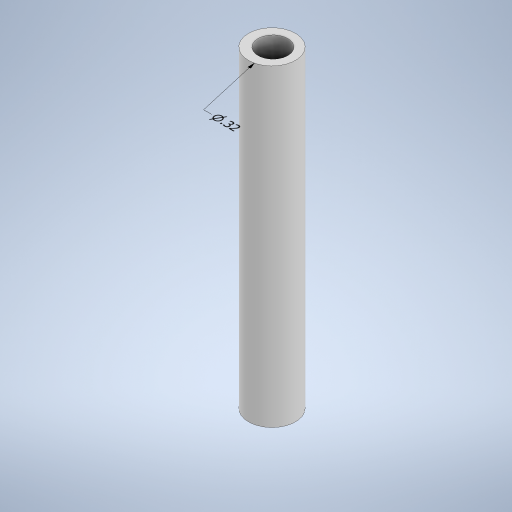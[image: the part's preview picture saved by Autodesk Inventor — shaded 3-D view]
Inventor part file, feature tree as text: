
AUTODESK INVENTOR PART (.ipt)
format: ipt  version: 2024 (Build 280153000, 153)  size: 582,656 bytes
history: native  units: in
note: dims shown in document units (in); Inventor stores cm internally (conversion verified against a paired STEP export)
features: other x4, sketch x3, hole x2, extrude x1, plane x1
ambient origin geometry x8: Origin, YZ Plane, XZ Plane, XY Plane, X Axis, Y Axis, Z Axis, Center Point
bodies: Solid1 (feature_tree)
feature tree (11):
  other  "Annotations"
  extrude  "Extrusion1"  Depth=2.1in TaperAngle=0.0deg
  plane  "Work Plane1"
  hole  "Hole1"  [1 undecoded]
  hole  "Hole2"  [1 undecoded]
  sketch  "Sketch1"  dims[d0=0.315in d1=2.1in d2=0.0in]
  sketch  "Sketch3"  dims[d3=-1.05in]
  sketch  "Sketch4"  dims[d21=0.2in d22=0.75in d23=5.0in d24=0.25in d25=0.5635in d26=0.4345in d27=0.0in d30=0.2in d31=0.75in d32=0.375in d33=0.25in d34=0.5635in d35=0.4345in d36=0.0in d39=1.4023in d40=0.3133in d41=0.2915in d42=0.315in d43=1.388in d44=0.315in d45=0.707in d46=0.315in d37=0.75in d38=0.8108in]
  other  "Diameter Dimension 1"
  other  "Diameter Dimension 2"
  other  "Diameter Dimension 3"
note: 2 required parameter values undecoded (feature->parameter linkage not recoverable at this tier; creation-order binding heuristic only, values carry confidence <= 0.55)
